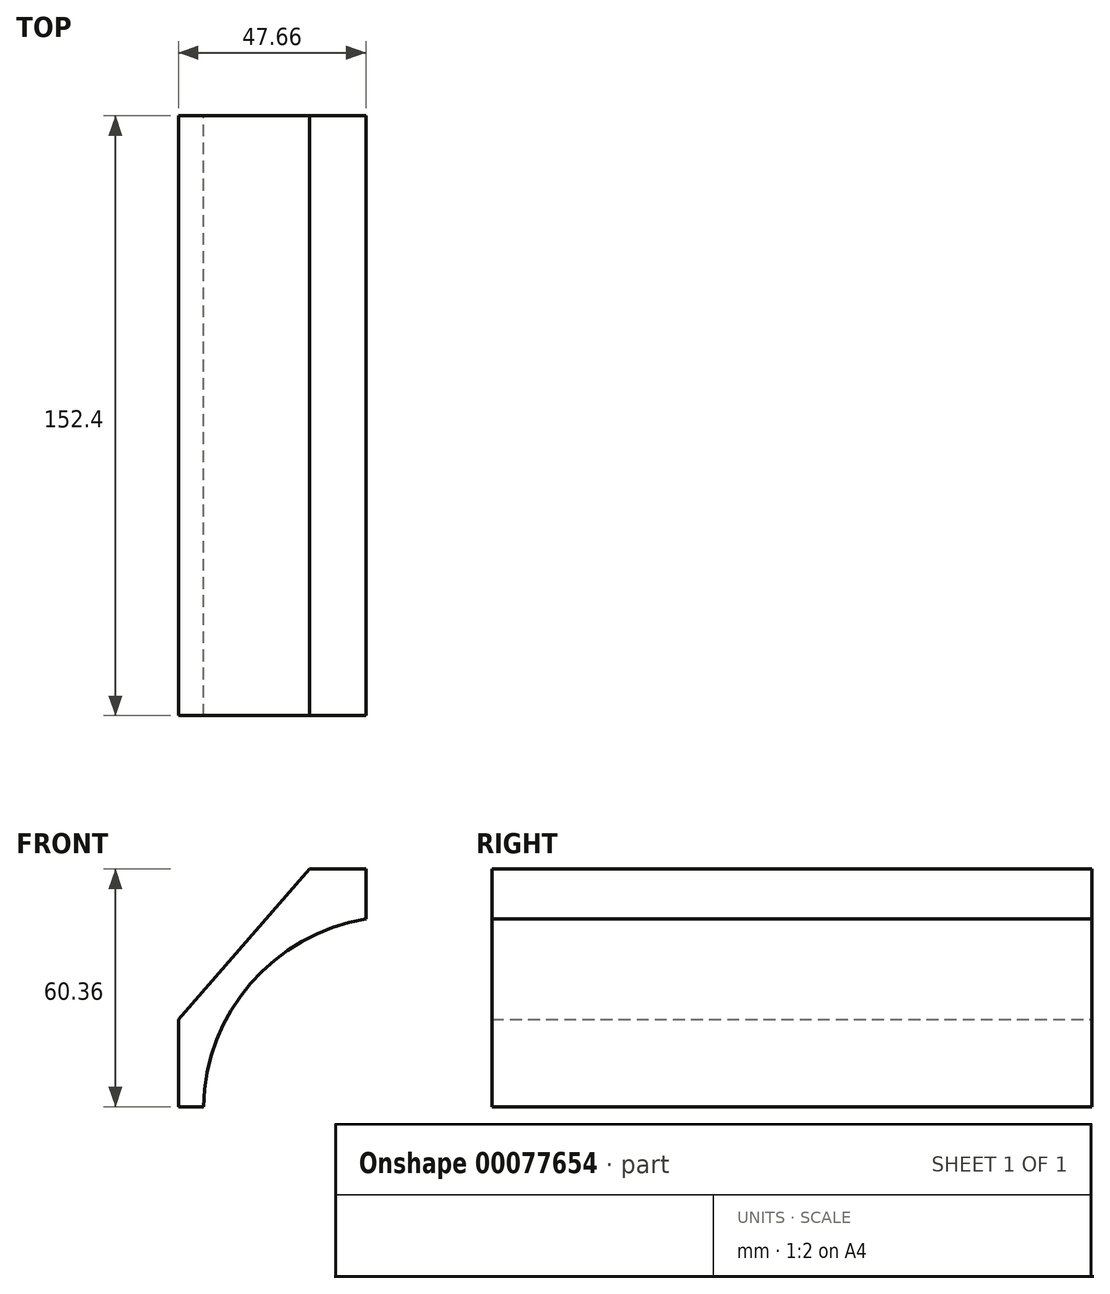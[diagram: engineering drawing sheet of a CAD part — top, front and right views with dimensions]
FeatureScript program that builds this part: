
annotation { "Feature Type Name" : "Feature", "Feature Type Description" : "" }
export const myFeature = defineFeature(function(context is Context, id is Id, definition is map)
    precondition{}
    {
        {
            var Q0;
            Q0=qCreatedBy(makeId("Front.planeOp"),FACE);
            var sketch = newSketch(context, id + "F0", { "sketchPlane" : qUnion([Q0])});
            skLineSegment(sketch, "E0", {"start": v(23.83, 30.18) * mm, "end": v(23.83, 17.47) * mm});
            skLineSegment(sketch, "E1", {"start": v(-23.83, -30.18) * mm, "end": v(-17.47, -30.18) * mm});
            skLineSegment(sketch, "E2", {"start": v(-23.83, -30.18) * mm, "end": v(-23.83, -7.94) * mm});
            skLineSegment(sketch, "E3", {"start": v(-23.83, -7.94) * mm, "end": v(9.46, 30.18) * mm});
            skLineSegment(sketch, "E4", {"start": v(9.46, 30.18) * mm, "end": v(23.83, 30.18) * mm});
            skArc(sketch, "E5", {"start": v(23.83, 17.47) * mm, "mid": v(-5.45, 1.12) * mm, "end": v(-17.47, -30.18) * mm});
            skSolve(sketch);
        }
        {
            var Q0;
            Q0=makeQuery(id+"F0.imprint","IMPRINT",FACE,{"disambiguationData":[TD([[makeQuery(id+"F0.imprint","IMPRINT",EDGE,{"derivedFrom":sQuery(id+"F0.wireOp",EDGE,"E0")}),-1.0]])]});
            extrude(context, id + "F1", {"entities" : qUnion([Q0]), "depth" : 152.4 * mm});
        }
    });
